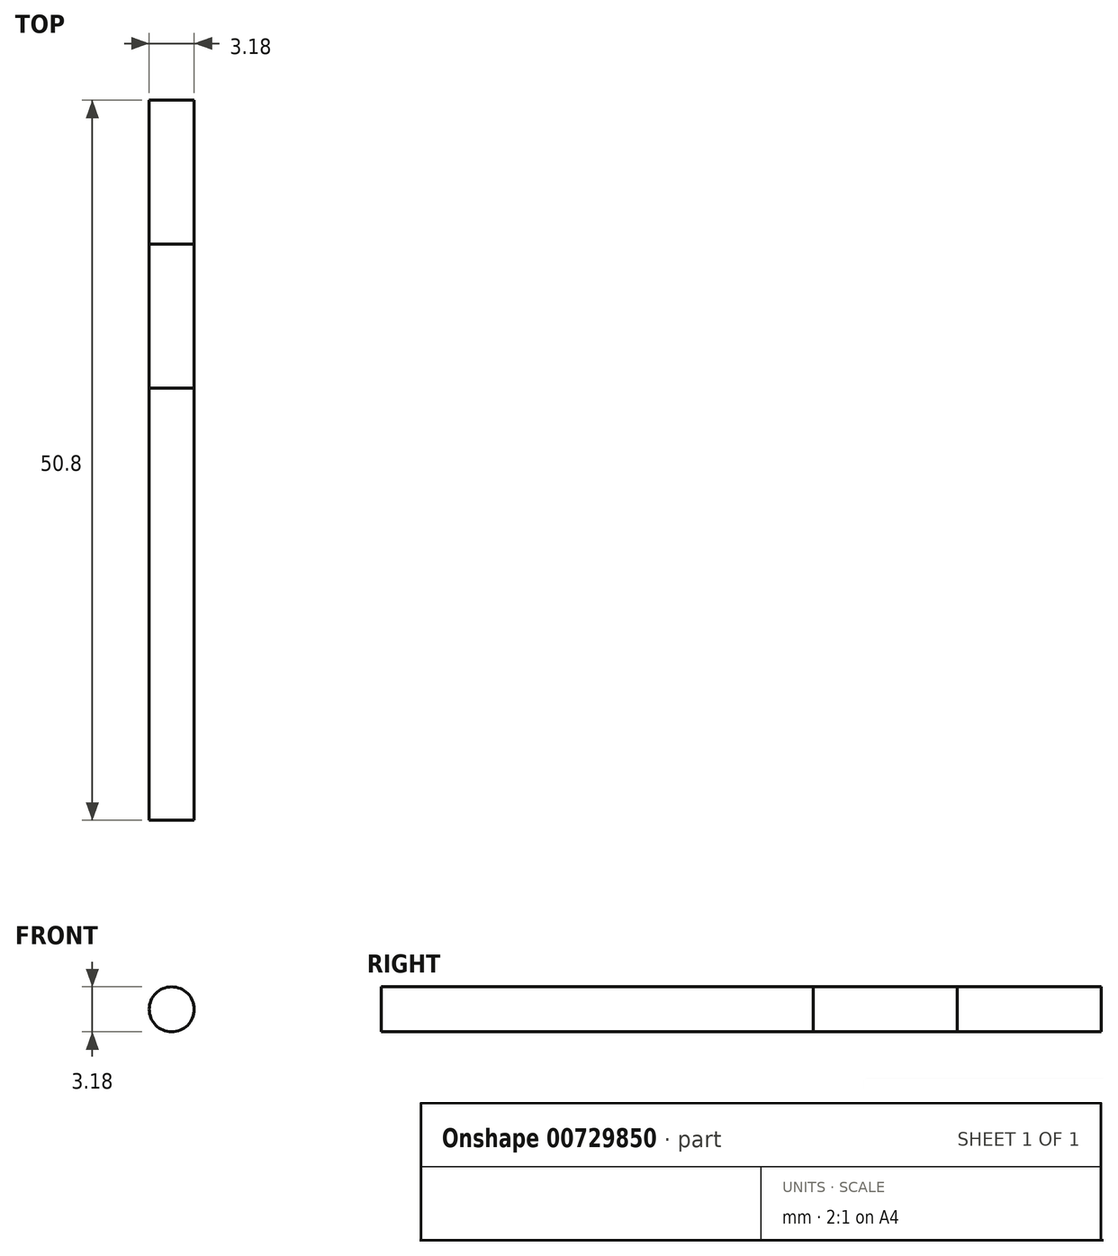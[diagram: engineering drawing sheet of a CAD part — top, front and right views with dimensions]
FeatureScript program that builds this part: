
annotation { "Feature Type Name" : "Feature", "Feature Type Description" : "" }
export const myFeature = defineFeature(function(context is Context, id is Id, definition is map)
    precondition{}
    {
        {
            var Q0;
            Q0=qCreatedBy(makeId("Front.planeOp"),FACE);
            var sketch = newSketch(context, id + "F0", { "sketchPlane" : qUnion([Q0])});
            skCircle(sketch, "E0", {"center": v(0, 0) * mm, "radius": 1.59 * mm});
            skSolve(sketch);
        }
        {
            var Q0;
            Q0=qSketchRegion(id+"F0",true);
            extrude(context, id + "F1", {"entities" : qUnion([Q0]), "depth" : 10.16 * mm, "offsetDistance" : 25.4 * mm});
        }
        {
            var Q0;
            Q0=makeQuery(id+"F1.opExtrude","CAP_FACE",FACE,{"disambiguationData":[OSD([sQuery(id+"F0.wireOp",EDGE,"E0")])],"isStart":false});
            extrude(context, id + "F2", {"entities" : qUnion([Q0]), "depth" : 10.16 * mm, "offsetDistance" : 25.4 * mm});
        }
        {
            var Q0;
            Q0=makeQuery(id+"F2.opExtrude","CAP_FACE",FACE,{"disambiguationData":[OSD([sQuery(id+"F0.wireOp",EDGE,"E0")])],"isStart":false});
            var sketch = newSketch(context, id + "F3", { "sketchPlane" : qUnion([Q0])});
            skCircle(sketch, "E1", {"center": v(0, 0) * mm, "radius": 1.59 * mm});
            skSolve(sketch);
        }
        {
            var Q0;
            Q0=makeQuery(id+"F3.imprint","IMPRINT",FACE,{"disambiguationData":[TD([[makeQuery(id+"F3.imprint","IMPRINT",EDGE,{"derivedFrom":sQuery(id+"F3.wireOp",EDGE,"E1")}),1.0]])]});
            extrude(context, id + "F4", {"entities" : qUnion([Q0]), "depth" : 30.48 * mm, "offsetDistance" : 25.4 * mm});
        }
    });
